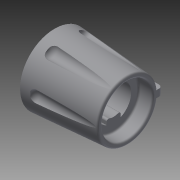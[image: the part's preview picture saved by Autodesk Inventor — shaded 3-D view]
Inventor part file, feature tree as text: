
AUTODESK INVENTOR PART (.ipt)
format: ipt  version: 2016 (Build 200138000, 138)  size: 318,464 bytes
history: native  units: mm
features: fillet x4, extrude x3, sketch x3, revolve x1, pattern_circular x1
ambient origin geometry x8: Origin, YZ Plane, XZ Plane, XY Plane, X Axis, Y Axis, Z Axis, Center Point
bodies: Solid1 (feature_tree)
feature tree (12):
  revolve  "Revolution1"  [1 undecoded]
  extrude  "Extrusion1"  TaperAngle=0.0deg  [1 undecoded]
  fillet  "Fillet2"  Radius=3.0mm
  sketch  "Sketch4"  dims[d2=5.0mm d3=0.0mm d4=3.0mm]
  extrude  "Extrusion2"  Depth=8.5mm
  fillet  "Fillet3"  [1 undecoded]
  fillet  "Fillet4"  Radius=3.5mm
  extrude  "Extrusion3"  Depth=2.0mm
  fillet  "Fillet5"  Radius=1.0mm
  pattern_circular  "Circular Pattern1"  [2 undecoded]
  sketch  "Sketch1"  dims[d0=2.5mm d1=3.7mm]
  sketch  "Sketch5"  dims[d5=0.0mm d8=8.5mm d9=90.0deg d10=3.5mm d11=2.0mm d12=1.0mm d13=1.75mm d14=4.0mm d15=0.0mm d16=2.0mm d17=3.6mm d18=0.698132mm d20=0.25mm d21=0.25mm d22=1.0mm d23=1.0mm d24=0.0mm d25=10.0mm d26=0.0mm d27=0.5mm d28=0.25mm d29=2.0mm d30=9.0mm d31=0.0mm d32=0.75mm d33=60.0mm d34=360.0deg]
note: 5 required parameter values undecoded (feature->parameter linkage not recoverable at this tier; creation-order binding heuristic only, values carry confidence <= 0.55)